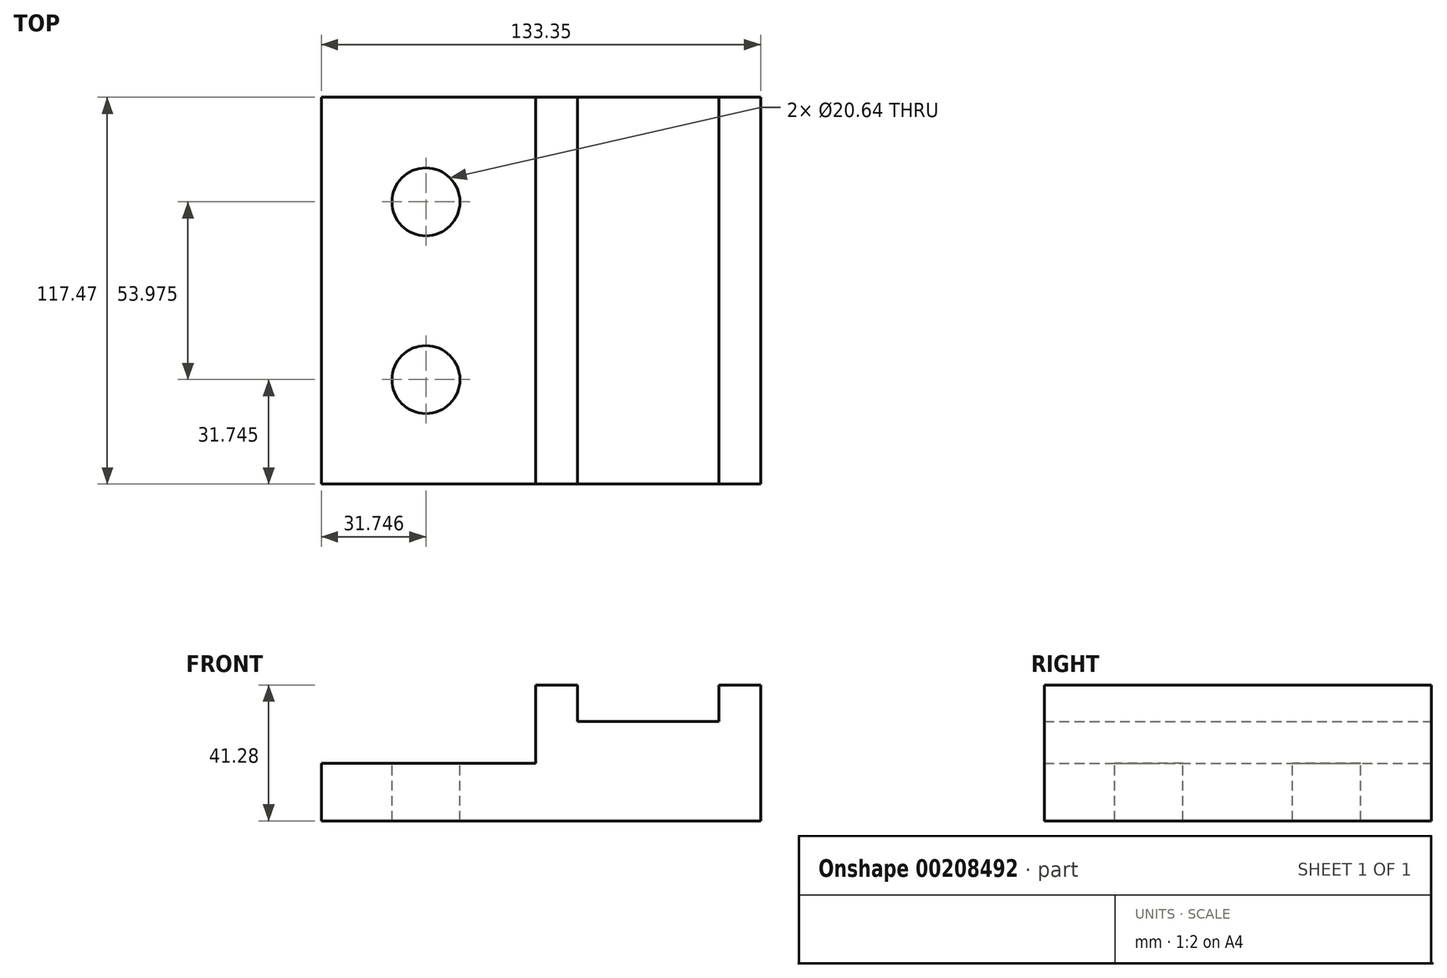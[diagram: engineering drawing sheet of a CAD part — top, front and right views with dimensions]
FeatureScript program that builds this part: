
annotation { "Feature Type Name" : "Feature", "Feature Type Description" : "" }
export const myFeature = defineFeature(function(context is Context, id is Id, definition is map)
    precondition{}
    {
        {
            var Q0;
            Q0=qCreatedBy(makeId("Front.planeOp"),FACE);
            var sketch = newSketch(context, id + "F0", { "sketchPlane" : qUnion([Q0])});
            skLineSegment(sketch, "E0", {"start": v(-75.24, 6.88) * mm, "end": v(-75.24, -10.58) * mm});
            skLineSegment(sketch, "E1", {"start": v(-75.24, -10.58) * mm, "end": v(58.1, -10.58) * mm});
            skLineSegment(sketch, "E2", {"start": v(58.1, -10.58) * mm, "end": v(58.1, 30.7) * mm});
            skLineSegment(sketch, "E3", {"start": v(58.1, 30.7) * mm, "end": v(45.4, 30.7) * mm});
            skLineSegment(sketch, "E4", {"start": v(45.4, 30.7) * mm, "end": v(45.4, 19.58) * mm});
            skLineSegment(sketch, "E5", {"start": v(2.54, 19.58) * mm, "end": v(45.4, 19.58) * mm});
            skLineSegment(sketch, "E6", {"start": v(2.54, 19.58) * mm, "end": v(2.54, 30.7) * mm});
            skLineSegment(sketch, "E7", {"start": v(2.54, 30.7) * mm, "end": v(-10.16, 30.7) * mm});
            skLineSegment(sketch, "E8", {"start": v(-10.16, 30.7) * mm, "end": v(-10.16, 6.88) * mm});
            skLineSegment(sketch, "E9", {"start": v(-10.16, 6.88) * mm, "end": v(-75.24, 6.88) * mm});
            skSolve(sketch);
        }
        {
            var Q0;
            Q0 = qSketchRegion(id + "F0", true);
            extrude(context, id + "F1", {"entities" : qUnion([Q0]), "depth" : 117.47 * mm});
        }
        {
            var Q0;
            Q0=makeQuery(id+"F1.opExtrude","SWEPT_FACE",FACE,{"disambiguationData":[OSD([sQuery(id+"F0.wireOp",EDGE,"E9")])]});
            var sketch = newSketch(context, id + "F2", { "sketchPlane" : qUnion([Q0])});
            skCircle(sketch, "E10", {"center": v(-43.5, -85.72) * mm, "radius": 10.32 * mm});
            skCircle(sketch, "E11", {"center": v(-43.5, -31.75) * mm, "radius": 10.32 * mm});
            skSolve(sketch);
        }
        {
            var Q0;
            Q0 = qSketchRegion(id + "F2", true);
            extrude(context, id + "F3", {"entities" : qUnion([Q0]), "operationType" : NewBodyOperationType.REMOVE, "endBound" : BoundingType.THROUGH_ALL, "oppositeDirection" : true, "depth" : 25.4 * mm});
        }
    });
